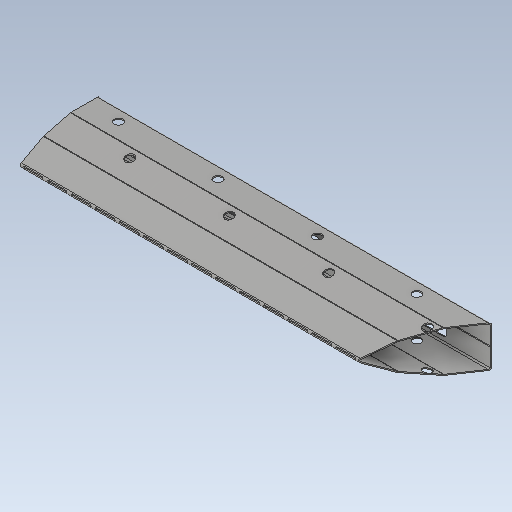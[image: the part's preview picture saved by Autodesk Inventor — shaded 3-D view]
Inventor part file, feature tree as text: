
AUTODESK INVENTOR PART (.ipt)
format: ipt  version: 2020.1 (Build 241239000, 239)  size: 876,544 bytes
history: native  units: mm
features: reference x24, other x23, sketch x16, sheet_metal_op x13, plane x9, projected_geometry x8, extrude x6
ambient origin geometry x8: Origin, YZ Plane, XZ Plane, XY Plane, X Axis, Y Axis, Z Axis, Center Point
bodies: Solid1 (feature_tree)
feature tree (99):
  plane  "Work Plane1"
  sheet_metal_op  "Face1"
  plane  "Work Plane2"
  sheet_metal_op  "Face2"
  plane  "Work Plane3"
  sheet_metal_op  "Face3"
  plane  "Work Plane4"
  sheet_metal_op  "Face4"
  plane  "Work Plane5"
  sheet_metal_op  "Face5"
  plane  "Work Plane6"
  sheet_metal_op  "Face6"
  plane  "Work Plane7"
  sheet_metal_op  "Face7"
  other  "midtplan"
  extrude  "afskær bund"  Depth=3.75mm
  extrude  "afskær top"  Depth=1.5mm
  extrude  "hulsæt til stifter"  Depth=3.75mm
  sketch  "Sketch14"  dims[d16=3.75mm]
  plane  "Work Plane12"
  extrude  "balusterhul"  Depth=3.0mm
  extrude  "balusterhul skråkompensering"  Depth=6.0mm
  extrude  "test"  Depth=3.75mm
  sketch  "Sketch1"  dims[d0=3.0mm d1=3.75mm]
  reference  "Reference1"
  reference  "Reference2"
  reference  "Reference3"
  reference  "Reference4"
  other  "Plate1"
  sketch  "Sketch2"  dims[d2=3.0mm d3=1.5mm]
  reference  "Reference5"
  reference  "Reference6"
  reference  "Reference7"
  reference  "Reference8"
  other  "Plate2"
  sheet_metal_op  "Bend1"
  sketch  "Sketch3"  dims[d4=6.0mm d5=3.75mm]
  reference  "Reference9"
  reference  "Reference10"
  reference  "Reference11"
  other  "Plate3"
  sheet_metal_op  "Bend2"
  sketch  "Sketch4"  dims[d6=3.75mm d7=3.0mm]
  reference  "Reference12"
  reference  "Reference13"
  reference  "Reference14"
  reference  "Reference15"
  other  "Plate4"
  sheet_metal_op  "Bend3"
  sketch  "Sketch5"  dims[d8=1.5mm d9=6.0mm]
  reference  "Reference16"
  reference  "Reference17"
  reference  "Reference18"
  other  "Plate5"
  sheet_metal_op  "Bend4"
  sketch  "Sketch6"  dims[d10=3.75mm d11=3.75mm]
  reference  "Reference19"
  reference  "Reference20"
  reference  "Reference21"
  other  "Plate6"
  sheet_metal_op  "Bend5"
  sketch  "Sketch7"  dims[d12=3.0mm]
  reference  "Reference22"
  reference  "Reference23"
  other  "Plate7"
  sheet_metal_op  "Bend6"
  sketch  "Sketch8"  dims[d13=1.5mm]
  reference  "Reference24"
  projected_geometry  "Projected Loop1"
  other  "huller til stifter"
  projected_geometry  "Projected Loop3"
  sketch  "Sketch12"  dims[d14=6.0mm]
  projected_geometry  "Projected Loop4"
  sketch  "Sketch13"  dims[d15=3.75mm]
  projected_geometry  "Projected Loop5"
  plane  "Work Plane11"
  sketch  "Sketch15"  dims[d17=3.0mm]
  sketch  "Sketch16"  dims[d18=1.5mm]
  projected_geometry  "Projected Loop6"
  projected_geometry  "Projected Loop7"
  sketch  "Sketch17"  dims[d19=6.0mm]
  projected_geometry  "Projected Loop8"
  projected_geometry  "Projected Loop9"
  sketch  "Sketch18"  dims[d20=3.75mm]
  sketch  "Sketch20"  dims[d21=3.75mm d22=3.0mm d23=1.5mm d24=6.0mm d25=3.75mm d26=3.75mm d27=3.0mm d28=1.5mm d29=6.0mm d30=3.75mm d31=3.0mm d32=0.0mm d33=3.0mm d39=250.0mm d41=33.7mm d42=33.7mm d43=60.0mm d44=70.0mm d45=16.85mm d46=65.0mm d47=60.0mm d48=10.0mm d49=0.0mm d50=250.0mm d51=33.7mm d52=33.7mm d53=60.0mm d54=16.85mm d55=65.0mm d56=60.0mm d57=30.0mm d59=302.736671mm d60=10.0mm d62=10.0mm d65=302.736671mm d66=195.343893mm d68=306.228mm d69=10.0mm d70=0.0mm d71=96.671937mm d74=10.0mm d75=0.0mm d76=5.986479mm d77=26.6mm d78=25.8mm d79=26.6mm d80=26.6mm d81=26.6mm d82=26.6mm d83=26.6mm d84=26.6mm d85=39.001254mm d95=113.170852mm d96=56.585426mm d97=90.0deg d98=49.5mm d99=100.0mm d100=0.0mm d101=2.046461mm d102=1.023231mm d103=10.0mm d104=0.0mm d105=90.0mm d106=342.765mm d107=342.765mm d108=30.0mm d109=30.0mm d110=30.0mm d111=342.765mm d112=10.0mm d113=3.0mm d114=0.0mm d115=6.0mm d116=61.0mm d117=8.0mm d118=150.0mm d120=73.2mm d121=10.0mm d123=10.0mm d125=3.0mm d126=0.0mm d129=10.0mm d130=0.0mm d131=1.0mm d132=1.0mm d133=1.0mm d134=1.0mm d135=140.0mm]
  other  "Cut1"
  other  "plantehuller"
  other  "bukkeperforering"
  parser-record x4  (decoder bookkeeping rows leaked as tree rows — omitted from the tree; the rows remain in map.json)
  other  "modul top.iam"
  other  "model:1"
  other  "Definition1"
  other  "modul.iam"
  other  "søjle+vange.iam"
  other  "stilladssøjle:2"
  other  "rør:1"
note: 4 file-system paths scrubbed to <path> (originals preserved in map.json)
